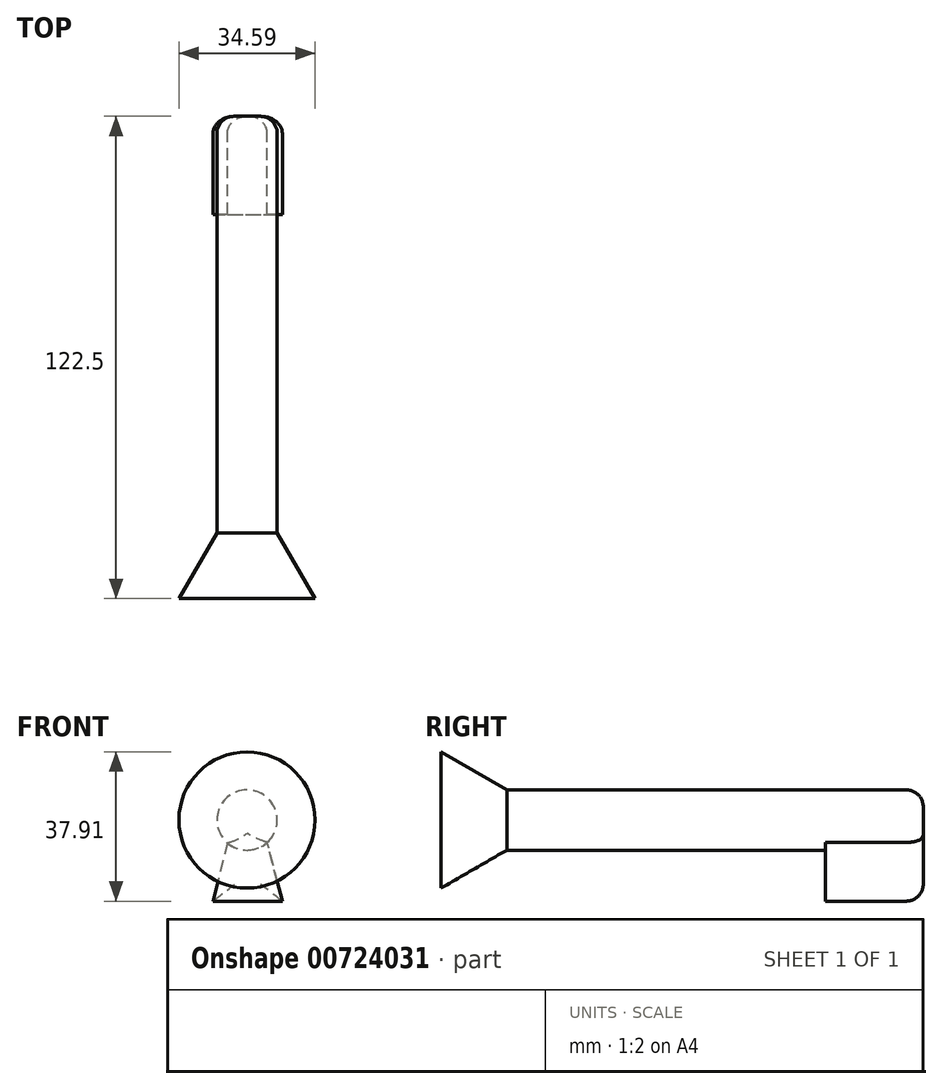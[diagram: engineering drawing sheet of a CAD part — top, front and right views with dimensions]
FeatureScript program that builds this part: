
annotation { "Feature Type Name" : "Feature", "Feature Type Description" : "" }
export const myFeature = defineFeature(function(context is Context, id is Id, definition is map)
    precondition{}
    {
        {
            var Q0;
            Q0=qCreatedBy(makeId("Front.planeOp"),FACE);
            var sketch = newSketch(context, id + "F0", { "sketchPlane" : qUnion([Q0])});
            skCircle(sketch, "E0", {"center": v(-0.1, 11.74) * mm, "radius": 7.65 * mm});
            skLineSegment(sketch, "E1", {"start": v(-5.07, 5.92) * mm, "end": v(-8.74, -8.87) * mm});
            skLineSegment(sketch, "E2", {"start": v(-8.74, -8.87) * mm, "end": v(8.86, -8.87) * mm});
            skLineSegment(sketch, "E3", {"start": v(8.86, -8.87) * mm, "end": v(5.04, 6.07) * mm});
            skSolve(sketch);
        }
        {
            var Q0;
            {var subQ0=sQuery(id+"F0.wireOp",EDGE,"E0");var subQ1=makeQuery(id+"F0.imprint","INTERSECT",VERTEX,{"derivedFrom":[subQ0,sQuery(id+"F0.wireOp",EDGE,"E1")]});Q0=makeQuery(id+"F0.imprint","IMPRINT",FACE,{"disambiguationData":[TD([[makeQuery(id+"F0.imprint","IMPRINT",EDGE,{"disambiguationData":[TD([[subQ1,-1.0]])],"derivedFrom":subQ0}),1.0]])]});}
            extrude(context, id + "F1", {"entities" : qUnion([Q0]), "depth" : 105.8 * mm, "offsetDistance" : 25 * mm});
        }
        {
            var Q0;
            {var subQ0=sQuery(id+"F0.wireOp",EDGE,"E1");Q0=makeQuery(id+"F0.imprint","IMPRINT",FACE,{"disambiguationData":[TD([[makeQuery(id+"F0.imprint","IMPRINT",EDGE,{"derivedFrom":subQ0}),1.0]])]});}
            extrude(context, id + "F2", {"entities" : qUnion([Q0]), "operationType" : NewBodyOperationType.ADD, "depth" : 24.9 * mm, "offsetDistance" : 25 * mm});
        }
        {
            var Q0;
            Q0=makeQuery(id+"F1.opExtrude","CAP_FACE",FACE,{"disambiguationData":[OSD([sQuery(id+"F0.wireOp",EDGE,"E0")])],"isStart":false});
            extrude(context, id + "F3", {"entities" : qUnion([Q0]), "operationType" : NewBodyOperationType.ADD, "depth" : 16.7 * mm, "offsetDistance" : 25 * mm, "hasDraft" : true, "draftAngle" : 30 * degree});
        }
        {
            var Q0;
            Q0=makeQuery(id+"F2.opExtrude","CAP_EDGE",EDGE,{"disambiguationData":[OSD([sQuery(id+"F0.wireOp",EDGE,"E2")])],"isStart":true});
            var Q1;
            Q1=makeQuery(id+"F2.opExtrude","CAP_EDGE",EDGE,{"disambiguationData":[OSD([sQuery(id+"F0.wireOp",EDGE,"E3")])],"isStart":true});
            var Q2;
            Q2=makeQuery(id+"F2.opExtrude","CAP_EDGE",EDGE,{"disambiguationData":[OSD([sQuery(id+"F0.wireOp",EDGE,"E1")])],"isStart":true});
            var Q3;
            Q3=makeQuery(id+"F1.opExtrude","CAP_EDGE",EDGE,{"disambiguationData":[OSD([sQuery(id+"F0.wireOp",EDGE,"E0")])],"isStart":true});
            fillet(context, id + "F4", {"entities" : qUnion([Q0, Q1, Q2, Q3]), "radius" : 4.3 * mm, "tangentPropagation" : true, "allowEdgeOverflow" : false});
        }
    });
